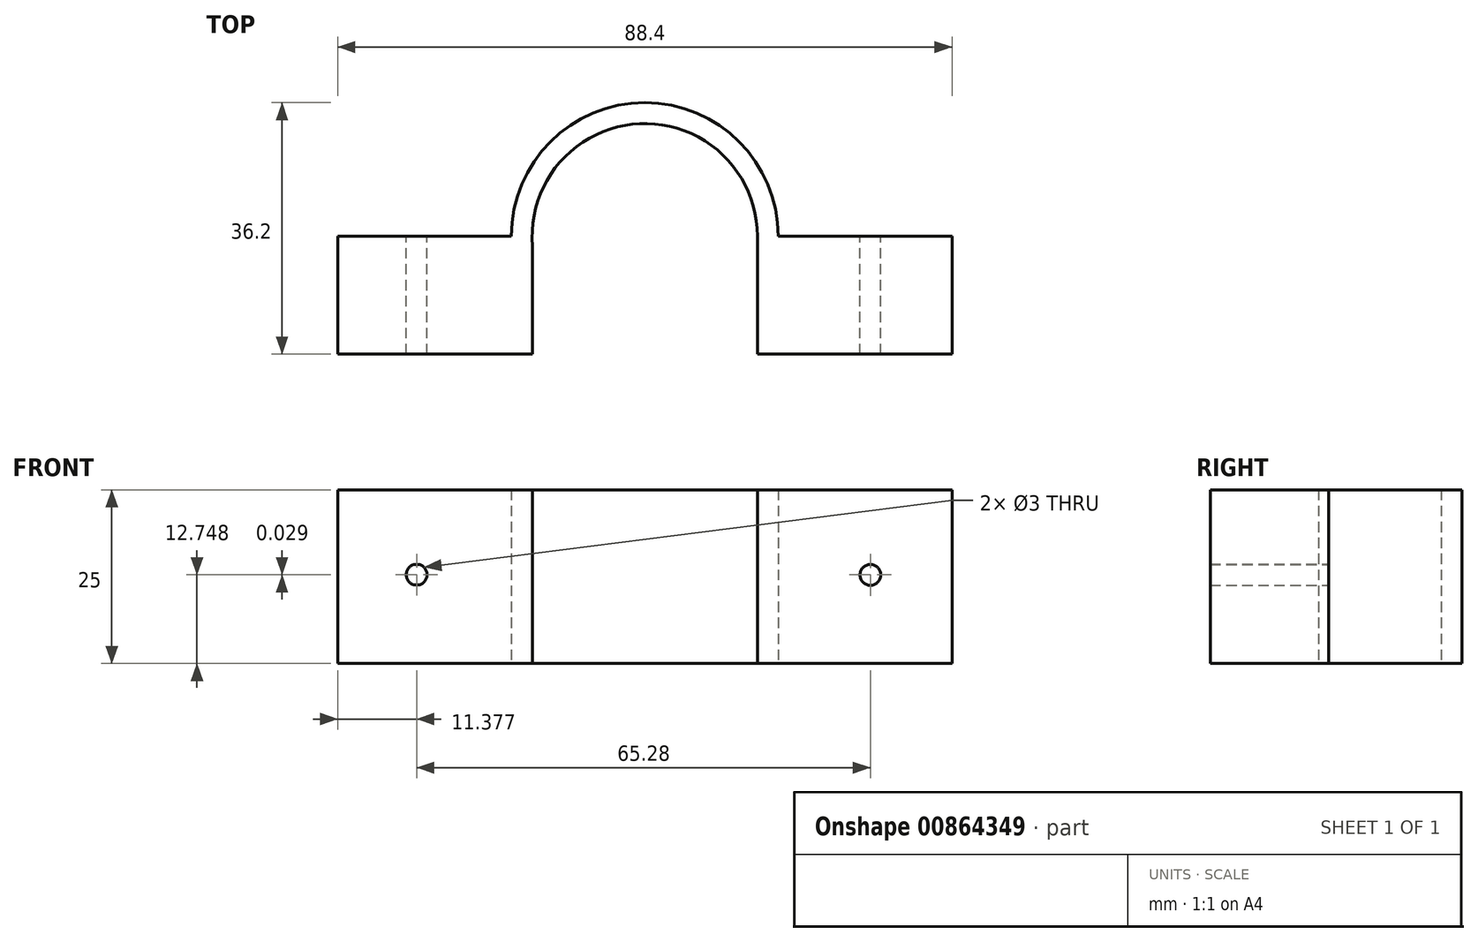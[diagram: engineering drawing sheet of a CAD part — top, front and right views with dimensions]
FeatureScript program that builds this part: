
annotation { "Feature Type Name" : "Feature", "Feature Type Description" : "" }
export const myFeature = defineFeature(function(context is Context, id is Id, definition is map)
    precondition{}
    {
        {
            var Q0;
            Q0=qCreatedBy(makeId("Top.planeOp"),FACE);
            var sketch = newSketch(context, id + "F0", { "sketchPlane" : qUnion([Q0])});
            skLineSegment(sketch, "E0", {"start": v(0, 0) * mm, "end": v(0, 17) * mm});
            skLineSegment(sketch, "E1", {"start": v(0, 17) * mm, "end": v(25, 17) * mm});
            skArc(sketch, "E2", {"start": v(63.4, 17) * mm, "mid": v(44.2, 36.2) * mm, "end": v(25, 17) * mm});
            skLineSegment(sketch, "E3", {"start": v(25, 17) * mm, "end": v(44.2, 17) * mm, "construction": true});
            skArc(sketch, "E4.0", {"start": v(60.34, 18.43) * mm, "mid": v(44.2, 33.2) * mm, "end": v(28.06, 18.43) * mm});
            skLineSegment(sketch, "E5", {"start": v(44.2, 17) * mm, "end": v(44.2, 33.2) * mm, "construction": true});
            skLineSegment(sketch, "E6.MirrorCS", {"start": v(88.4, 0) * mm, "end": v(88.4, 17) * mm});
            skLineSegment(sketch, "E7.MirrorCS", {"start": v(88.4, 17) * mm, "end": v(63.4, 17) * mm});
            skLineSegment(sketch, "E8", {"start": v(0, 0) * mm, "end": v(88.4, 0) * mm});
            skArc(sketch, "E9", {"start": v(28.06, 18.43) * mm, "mid": v(44.2, 0.8) * mm, "end": v(60.34, 18.43) * mm});
            skLineSegment(sketch, "E10", {"start": v(28.06, 17) * mm, "end": v(28.06, 0) * mm});
            skLineSegment(sketch, "E11", {"start": v(60.4, 17) * mm, "end": v(60.4, 0) * mm});
            skSolve(sketch);
        }
        {
            var Q0;
            {var subQ7=sQuery(id+"F0.wireOp",EDGE,"E0");Q0=makeQuery(id+"F0.imprint","IMPRINT",FACE,{"disambiguationData":[TD([[makeQuery(id+"F0.imprint","IMPRINT",EDGE,{"derivedFrom":subQ7}),-1.0]])]});}
            extrude(context, id + "F1", {"entities" : qUnion([Q0]), "depth" : 25 * mm, "offsetDistance" : 25 * mm});
        }
        {
            var Q0;
            Q0=makeQuery(id+"F1.opExtrude","SWEPT_FACE",FACE,{"disambiguationData":[OSD([sQuery(id+"F0.wireOp",EDGE,"E1")])]});
            var sketch = newSketch(context, id + "F2", { "sketchPlane" : qUnion([Q0])});
            skCircle(sketch, "E12", {"center": v(-11.38, 12.78) * mm, "radius": 1.5 * mm});
            skCircle(sketch, "E13", {"center": v(-76.66, 12.75) * mm, "radius": 1.5 * mm});
            skSolve(sketch);
        }
        {
            var Q0;
            Q0 = qSketchRegion(id + "F2", true);
            extrude(context, id + "F3", {"entities" : qUnion([Q0]), "operationType" : NewBodyOperationType.REMOVE, "oppositeDirection" : true, "depth" : 25 * mm, "offsetDistance" : 25 * mm});
        }
    });
